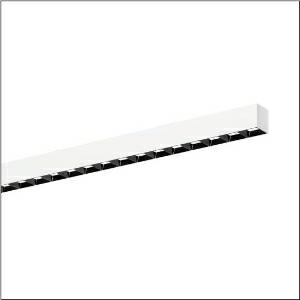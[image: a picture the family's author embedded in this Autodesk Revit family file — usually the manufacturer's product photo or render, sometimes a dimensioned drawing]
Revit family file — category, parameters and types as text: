
# Revit family: silica_r__21_51mx22tctaw_24f4
name_source: partatom
category: Lighting Fixtures
units: mm (PartAtom-declared; Revit-internal decimal feet)

## family parameters
Cut with Voids When Loaded = No
Host = Face
Light Source = No
Part Type = Normal
Room Calculation Point = No
Round Connector Dimension = Use Diameter
Shared = No

## types (1)
- --- (1 x LED, 9300 lm, 80.4 W, 6500K)
    Apparent Load = 80 VA
    CIE Flux Codes = 84 100 100 100 100
    Color Rendering = 80
    Color Temperature = 6500K
    Default Elevation = 1800 mm
    Description = Silica® 21, office luminaire, primary light control with darklight reflector, of PMMA, black, CAT 2 (L<= 3000cd/m²), light emission: direct distribution, primary light characteristic: symmetric, installation type: surface-mounted, LED, rated luminous flux: 9.300lm, luminous efficacy: 110lm/W, light colour: 8tw, colour temperature: 2700..6500K, control gear: DALI DT8, with terminal, 3+2-pole, max. 2.5mm², mains connection: 220..240V, AC, 50/60Hz, rated input power: 84.5W, luminaire housing, of aluminium, traffic white (RAL 9016), length: 3.004mm, width: 53mm, height: 53mm, protection rating (complete): IP20, insulation class (complete): insulation class I (protective earthing), certification: CE, permissible operating ambient temperature: 0..+35°C, standard: EN 50419, packaging unit: 1 piece
    Height = 53 mm
    Lamp = 1 x LED
    Lamp Light Flux = 9300 lm
    Lamp Power = 80.4 W
    Lamp count = 1
    Length = 3004 mm
    Luminous efficacy = 116 lm/W
    Manufacturer = Siteco
    ModVariant = No
    Model = 51MX22TCTAW
    Mounting Place = Ceiling
    Mounting Type = Surface mounted
    Number of Poles = 1
    OnlyDefault = Yes
    Power Factor = 1
    Product Name = Silica® 21
    Product group = office luminaire | ceiling mounted
    ProductGroupID = 302
    Protection Class = Protection class I
    Protection Degree = IP 20
    RLX_Detail_Level = 1
    RLX_Emergency_Light_Flux = 0 lm
    RLX_Emergency_Type = 0
    RLX_Emergency_Type_DB = No
    RlxData = <blob elided: 58981 chars, md5=5b26fbf9>
    Socket = socket
    Standby Power = 0 W
    System Light Flux = 9300 lm
    System Power = 80 W
    Type Comments = individual setting
    Type Image = l_1335873.jpg
    URL = http://relux.com
    VarID = @adj_140148
    Voltage = 0 V
    Weight = 0.00 kg
    Width = 53 mm

## geometry (parser evidence)
native form markers: Blend x4, Sweep x10
no freeform markers — native parametric forms only
